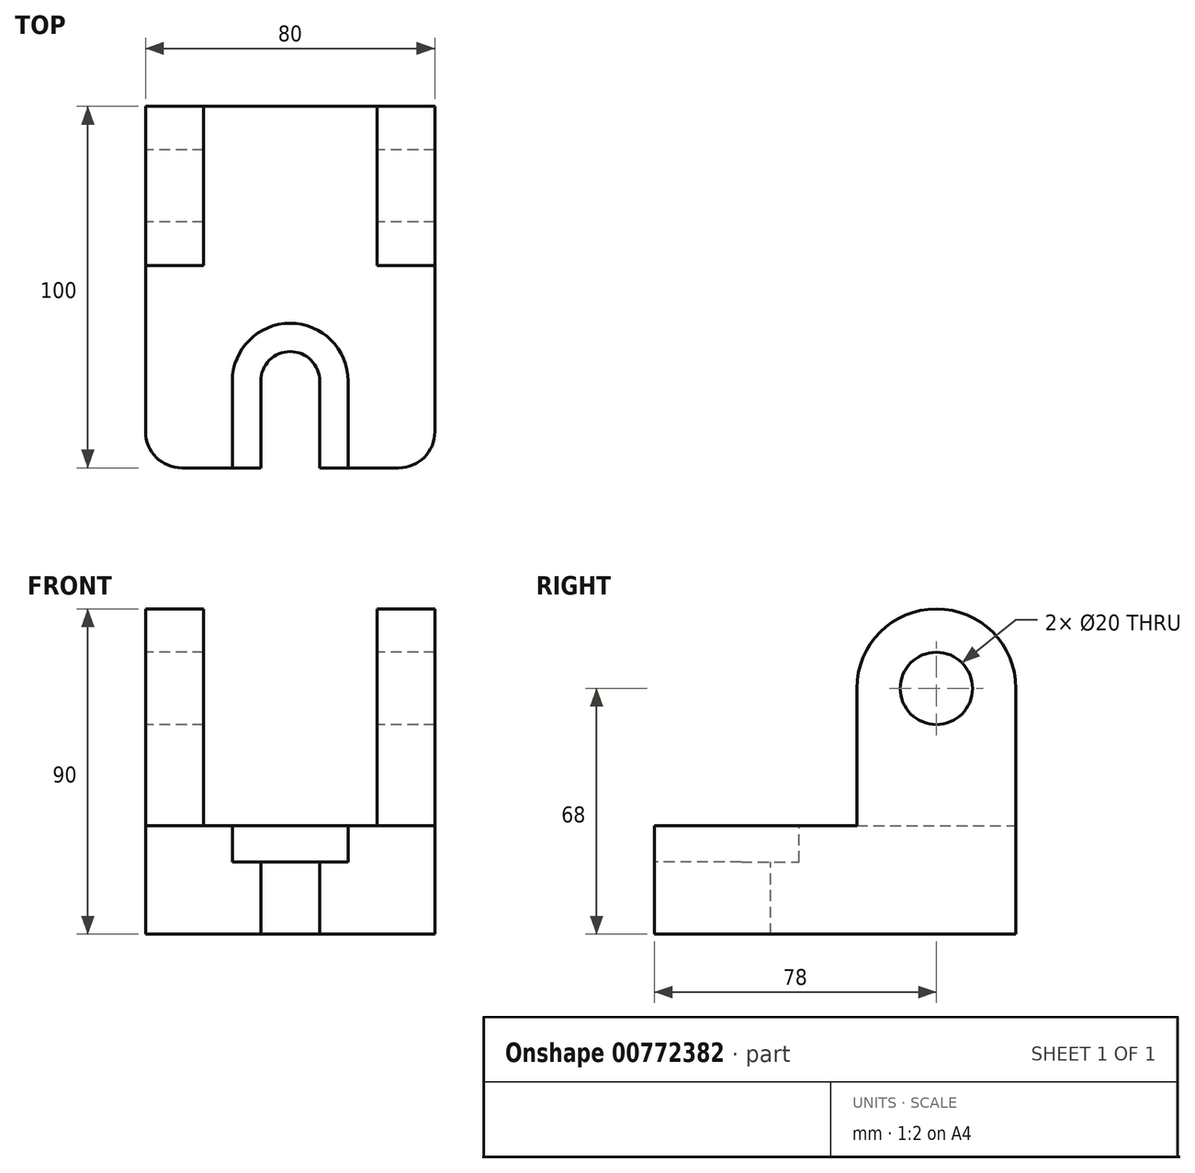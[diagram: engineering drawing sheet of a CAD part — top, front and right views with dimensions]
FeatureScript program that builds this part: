
annotation { "Feature Type Name" : "Feature", "Feature Type Description" : "" }
export const myFeature = defineFeature(function(context is Context, id is Id, definition is map)
    precondition{}
    {
        {
            var Q0;
            Q0=qCreatedBy(makeId("Right.planeOp"),FACE);
            var sketch = newSketch(context, id + "F0", { "sketchPlane" : qUnion([Q0])});
            skLineSegment(sketch, "E0", {"start": v(0, 0) * mm, "end": v(0, 30) * mm});
            skLineSegment(sketch, "E1", {"start": v(0, 30) * mm, "end": v(100, 30) * mm});
            skLineSegment(sketch, "E2", {"start": v(100, 30) * mm, "end": v(100, 0) * mm});
            skLineSegment(sketch, "E3", {"start": v(100, 0) * mm, "end": v(0, 0) * mm});
            skLineSegment(sketch, "E4", {"start": v(56, 30) * mm, "end": v(56, 68) * mm});
            skLineSegment(sketch, "E5", {"start": v(56, 68) * mm, "end": v(100, 68) * mm, "construction": true});
            skLineSegment(sketch, "E6", {"start": v(100, 68) * mm, "end": v(100, 30) * mm});
            skCircle(sketch, "E7", {"center": v(78, 68) * mm, "radius": 22 * mm});
            skCircle(sketch, "E8", {"center": v(78, 68) * mm, "radius": 10 * mm});
            skSolve(sketch);
        }
        {
            var Q0;
            Q0 = qSketchRegion(id + "F0", true);
            extrude(context, id + "F1", {"entities" : qUnion([Q0]), "endBound" : BoundingType.SYMMETRIC, "depth" : 80 * mm, "offsetDistance" : 25 * mm});
        }
        {
            var Q0;
            {var subQ2=sQuery(id+"F0.wireOp",EDGE,"E4");Q0=makeQuery(id+"F0.imprint","IMPRINT",FACE,{"disambiguationData":[TD([[makeQuery(id+"F0.imprint","IMPRINT",EDGE,{"derivedFrom":subQ2}),-1.0]])]});}
            var Q1;
            Q1=makeQuery(id+"F0.imprint","IMPRINT",FACE,{"disambiguationData":[TD([[makeQuery(id+"F0.imprint","IMPRINT",EDGE,{"derivedFrom":sQuery(id+"F0.wireOp",EDGE,"E8")}),-1.0]])]});
            extrude(context, id + "F2", {"entities" : qUnion([Q0, Q1]), "operationType" : NewBodyOperationType.REMOVE, "endBound" : BoundingType.SYMMETRIC, "oppositeDirection" : true, "depth" : 48 * mm, "offsetDistance" : 25 * mm});
        }
        {
            var Q0;
            {var subQ0=sQuery(id+"F0.wireOp",EDGE,"E1");Q0=makeQuery(id+"F2.boolean.opBoolean","MERGE",FACE,{"derivedFrom":[makeQuery(id+"F1.opExtrude","SWEPT_FACE",FACE,{"disambiguationData":[OSD([subQ0])]}),makeQuery(id+"F2.opExtrude","SWEPT_FACE",FACE,{"disambiguationData":[OSD([subQ0])]})]});}
            var sketch = newSketch(context, id + "F3", { "sketchPlane" : qUnion([Q0])});
            skLineSegment(sketch, "E9.bottom", {"start": v(-16, 24) * mm, "end": v(16, 24) * mm, "construction": true});
            skLineSegment(sketch, "E9.top", {"start": v(-16, -24) * mm, "end": v(16, -24) * mm});
            skLineSegment(sketch, "E9.left", {"start": v(-16, 24) * mm, "end": v(-16, -24) * mm});
            skLineSegment(sketch, "E9.right", {"start": v(16, 24) * mm, "end": v(16, -24) * mm});
            skPoint(sketch, "E9.middle", {"position": v(0, 0) * mm});
            skArc(sketch, "E10", {"start": v(16, 24) * mm, "mid": v(0, 40) * mm, "end": v(-16, 24) * mm});
            skLineSegment(sketch, "E11.0", {"start": v(-19, 51) * mm, "end": v(-35, 51) * mm});
            skLineSegment(sketch, "E11.1", {"start": v(-19, 95) * mm, "end": v(-19, 51) * mm});
            skLineSegment(sketch, "E11.2", {"start": v(-35, 51) * mm, "end": v(-35, 5) * mm});
            skLineSegment(sketch, "E11.3", {"start": v(19, 95) * mm, "end": v(-19, 95) * mm});
            skLineSegment(sketch, "E11.4", {"start": v(-35, 5) * mm, "end": v(35, 5) * mm});
            skLineSegment(sketch, "E11.5", {"start": v(35, 5) * mm, "end": v(35, 51) * mm});
            skLineSegment(sketch, "E11.6", {"start": v(35, 51) * mm, "end": v(19, 51) * mm});
            skLineSegment(sketch, "E11.7", {"start": v(19, 51) * mm, "end": v(19, 95) * mm});
            skLineSegment(sketch, "E12.0", {"start": v(-8.16, 24) * mm, "end": v(-8.16, -24) * mm});
            skArc(sketch, "E12.1", {"start": v(8.16, 24) * mm, "mid": v(0, 32.16) * mm, "end": v(-8.16, 24) * mm});
            skLineSegment(sketch, "E12.2", {"start": v(8.16, 24) * mm, "end": v(8.16, -24) * mm});
            skSolve(sketch);
        }
        {
            var Q0;
            {var subQ0=sQuery(id+"F3.wireOp",EDGE,"E11.4");var subQ1=sQuery(id+"F3.wireOp",EDGE,"E9.left");var subQ2=makeQuery(id+"F3.imprint","INTERSECT",VERTEX,{"derivedFrom":[subQ1,subQ0]});Q0=makeQuery(id+"F3.imprint","IMPRINT",FACE,{"disambiguationData":[TD([[makeQuery(id+"F3.imprint","IMPRINT",EDGE,{"disambiguationData":[TD([[subQ2,-1.0]])],"derivedFrom":subQ0}),-1.0]])]});}
            var Q1;
            {var subQ8=sQuery(id+"F3.wireOp",EDGE,"E10");Q1=makeQuery(id+"F3.imprint","IMPRINT",FACE,{"disambiguationData":[TD([[makeQuery(id+"F3.imprint","IMPRINT",EDGE,{"derivedFrom":subQ8}),1.0]])]});}
            var Q2;
            {var subQ0=sQuery(id+"F3.wireOp",EDGE,"E11.4");var subQ1=sQuery(id+"F3.wireOp",EDGE,"E9.right");var subQ2=makeQuery(id+"F3.imprint","INTERSECT",VERTEX,{"derivedFrom":[subQ1,subQ0]});Q2=makeQuery(id+"F3.imprint","IMPRINT",FACE,{"disambiguationData":[TD([[makeQuery(id+"F3.imprint","IMPRINT",EDGE,{"disambiguationData":[TD([[subQ2,1.0]])],"derivedFrom":subQ0}),-1.0]])]});}
            var Q3;
            {var subQ0=sQuery(id+"F3.wireOp",EDGE,"E12.0");var subQ1=sQuery(id+"F3.wireOp",EDGE,"E11.4");var subQ2=makeQuery(id+"F3.imprint","INTERSECT",VERTEX,{"derivedFrom":[subQ1,subQ0]});Q3=makeQuery(id+"F3.imprint","IMPRINT",FACE,{"disambiguationData":[TD([[makeQuery(id+"F3.imprint","IMPRINT",EDGE,{"disambiguationData":[TD([[subQ2,-1.0]])],"derivedFrom":subQ1}),-1.0]])]});}
            var Q4;
            {var subQ5=sQuery(id+"F3.wireOp",EDGE,"E12.1");Q4=makeQuery(id+"F3.imprint","IMPRINT",FACE,{"disambiguationData":[TD([[makeQuery(id+"F3.imprint","IMPRINT",EDGE,{"derivedFrom":subQ5}),1.0]])]});}
            extrude(context, id + "F4", {"entities" : qUnion([Q0, Q1, Q2, Q3, Q4]), "operationType" : NewBodyOperationType.REMOVE, "oppositeDirection" : true, "depth" : 10 * mm, "offsetDistance" : 25 * mm});
        }
        {
            var Q0;
            {var subQ5=sQuery(id+"F3.wireOp",EDGE,"E12.1");Q0=makeQuery(id+"F3.imprint","IMPRINT",FACE,{"disambiguationData":[TD([[makeQuery(id+"F3.imprint","IMPRINT",EDGE,{"derivedFrom":subQ5}),1.0]])]});}
            var Q1;
            {var subQ0=sQuery(id+"F3.wireOp",EDGE,"E12.0");var subQ1=sQuery(id+"F3.wireOp",EDGE,"E11.4");var subQ2=makeQuery(id+"F3.imprint","INTERSECT",VERTEX,{"derivedFrom":[subQ1,subQ0]});Q1=makeQuery(id+"F3.imprint","IMPRINT",FACE,{"disambiguationData":[TD([[makeQuery(id+"F3.imprint","IMPRINT",EDGE,{"disambiguationData":[TD([[subQ2,-1.0]])],"derivedFrom":subQ1}),-1.0]])]});}
            var Q2;
            {var subQ0=sQuery(id+"F3.wireOp",EDGE,"E12.0");var subQ1=sQuery(id+"F3.wireOp",EDGE,"E9.top");var subQ2=makeQuery(id+"F3.imprint","INTERSECT",VERTEX,{"derivedFrom":[subQ1,subQ0]});Q2=makeQuery(id+"F3.imprint","IMPRINT",FACE,{"disambiguationData":[TD([[makeQuery(id+"F3.imprint","IMPRINT",EDGE,{"disambiguationData":[TD([[subQ2,-1.0]])],"derivedFrom":subQ1}),1.0]])]});}
            var Q3;
            Q3=makeQuery(id+"F1.opExtrude","SWEPT_FACE",FACE,{"disambiguationData":[OSD([sQuery(id+"F0.wireOp",EDGE,"E3")])]});
            extrude(context, id + "F5", {"entities" : qUnion([Q0, Q1, Q2]), "operationType" : NewBodyOperationType.REMOVE, "endBound" : BoundingType.UP_TO_SURFACE, "oppositeDirection" : true, "depth" : 25 * mm, "endBoundEntityFace" : qUnion([Q3]), "offsetDistance" : 25 * mm});
        }
        {
            var Q0;
            Q0=makeQuery(id+"F1.opExtrude","CAP_EDGE",EDGE,{"disambiguationData":[OSD([sQuery(id+"F0.wireOp",EDGE,"E0")])],"isStart":true});
            var Q1;
            Q1=makeQuery(id+"F1.opExtrude","CAP_EDGE",EDGE,{"disambiguationData":[OSD([sQuery(id+"F0.wireOp",EDGE,"E0")])],"isStart":false});
            fillet(context, id + "F6", {"entities" : qUnion([Q0, Q1]), "radius" : 10 * mm, "tangentPropagation" : true, "allowEdgeOverflow" : false});
        }
    });
